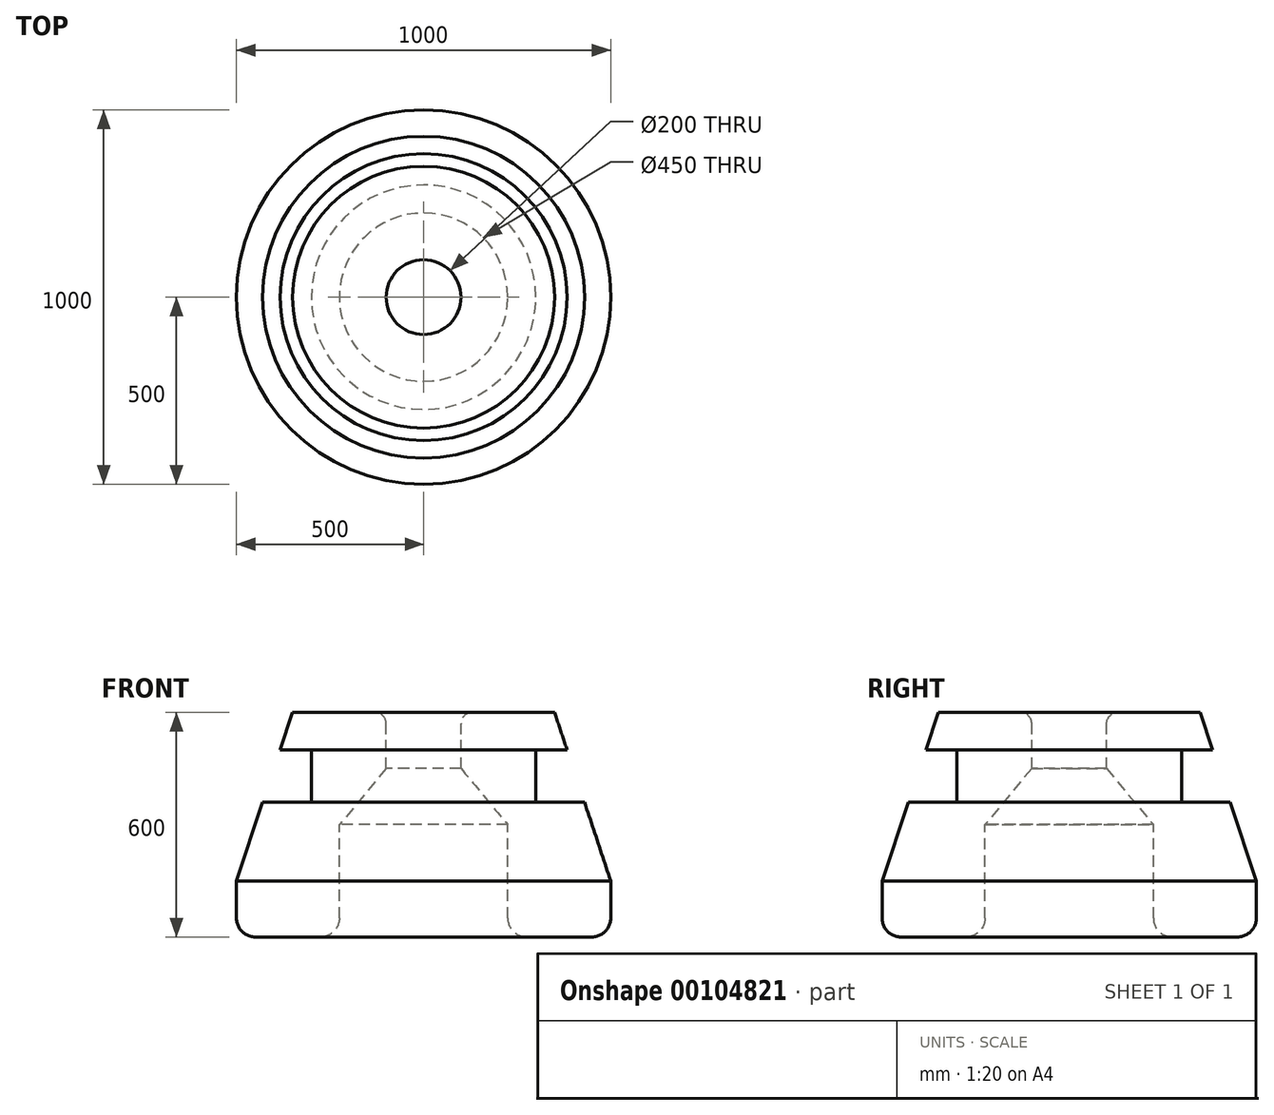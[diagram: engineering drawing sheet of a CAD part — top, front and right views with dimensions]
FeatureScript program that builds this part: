
annotation { "Feature Type Name" : "Feature", "Feature Type Description" : "" }
export const myFeature = defineFeature(function(context is Context, id is Id, definition is map)
    precondition{}
    {
        {
            var Q0;
            Q0=qCreatedBy(makeId("Front.planeOp"),FACE);
            var sketch = newSketch(context, id + "F0", { "sketchPlane" : qUnion([Q0])});
            skPoint(sketch, "E0", {"position": v(0, 0) * mm});
            skLineSegment(sketch, "E1.bottom", {"start": v(100, 300) * mm, "end": v(350, 300) * mm});
            skLineSegment(sketch, "E1.top", {"start": v(225, -300) * mm, "end": v(500, -300) * mm});
            skLineSegment(sketch, "E1.right", {"start": v(500, -150) * mm, "end": v(500, -300) * mm});
            skPoint(sketch, "E2", {"position": v(350, 300) * mm});
            skPoint(sketch, "E3", {"position": v(500, -150) * mm});
            skLineSegment(sketch, "E4", {"start": v(350, 300) * mm, "end": v(383.33, 200) * mm});
            skPoint(sketch, "E5", {"position": v(300, -300) * mm});
            skPoint(sketch, "E6", {"position": v(500, -300) * mm});
            skPoint(sketch, "E7", {"position": v(300, 60) * mm});
            skPoint(sketch, "E8", {"position": v(300, 200) * mm});
            skLineSegment(sketch, "E9", {"start": v(300, 200) * mm, "end": v(383.33, 200) * mm});
            skLineSegment(sketch, "E10", {"start": v(300, 200) * mm, "end": v(300, 60) * mm});
            skLineSegment(sketch, "E11", {"start": v(300, 60) * mm, "end": v(430, 60) * mm});
            skLineSegment(sketch, "E12.trimOffspring", {"start": v(430, 60) * mm, "end": v(500, -150) * mm});
            skPoint(sketch, "E13", {"position": v(100, 300) * mm});
            skPoint(sketch, "E14", {"position": v(100, 150) * mm});
            skLineSegment(sketch, "E15", {"start": v(100, 300) * mm, "end": v(100, 150) * mm});
            skPoint(sketch, "E16", {"position": v(225, -300) * mm});
            skPoint(sketch, "E17", {"position": v(0, -300) * mm});
            skPoint(sketch, "E18", {"position": v(225, 0) * mm});
            skLineSegment(sketch, "E19", {"start": v(100, 150) * mm, "end": v(225, 0) * mm});
            skLineSegment(sketch, "E20", {"start": v(225, 0) * mm, "end": v(225, -300) * mm});
            skPoint(sketch, "E21.end.orphan", {"position": v(0, 150) * mm});
            skPoint(sketch, "E22.orphan", {"position": v(0, 300) * mm});
            skLineSegment(sketch, "E23", {"start": v(100, 300) * mm, "end": v(0, 300) * mm, "construction": true});
            skLineSegment(sketch, "E24", {"start": v(0, 300) * mm, "end": v(0, -300) * mm, "construction": true});
            skLineSegment(sketch, "E25", {"start": v(0, -300) * mm, "end": v(225, -300) * mm, "construction": true});
            skSolve(sketch);
        }
        {
            var Q0;
            Q0 = qSketchRegion(id + "F0", true);
            var Q1;
            Q1=sQuery(id+"F0.wireOp",EDGE,"E24");
            revolve(context, id + "F1", {"entities" : qUnion([Q0]), "axis" : qUnion([Q1]), "revolveType" : RevolveType.FULL});
        }
        {
            var Q0;
            Q0=makeQuery(id+"F1.opRevolve","SWEPT_EDGE",EDGE,{"disambiguationData":[OSD([sQuery(id+"F0.wireOp",EDGE,"E1.bottom"),sQuery(id+"F0.wireOp",EDGE,"E15")])]});
            fillet(context, id + "F2", {"entities" : qUnion([Q0]), "radius" : 30 * mm, "tangentPropagation" : true, "allowEdgeOverflow" : false});
        }
        {
            var Q0;
            Q0=makeQuery(id+"F1.opRevolve","SWEPT_EDGE",EDGE,{"disambiguationData":[OSD([sQuery(id+"F0.wireOp",EDGE,"E1.top"),sQuery(id+"F0.wireOp",EDGE,"E1.right")])]});
            fillet(context, id + "F3", {"entities" : qUnion([Q0]), "radius" : 50 * mm, "tangentPropagation" : true, "allowEdgeOverflow" : false});
        }
        {
            var Q0;
            Q0=makeQuery(id+"F1.opRevolve","SWEPT_EDGE",EDGE,{"disambiguationData":[OSD([sQuery(id+"F0.wireOp",EDGE,"E1.top"),sQuery(id+"F0.wireOp",EDGE,"E20")])]});
            fillet(context, id + "F4", {"entities" : qUnion([Q0]), "radius" : 50 * mm, "tangentPropagation" : true, "allowEdgeOverflow" : false});
        }
    });
